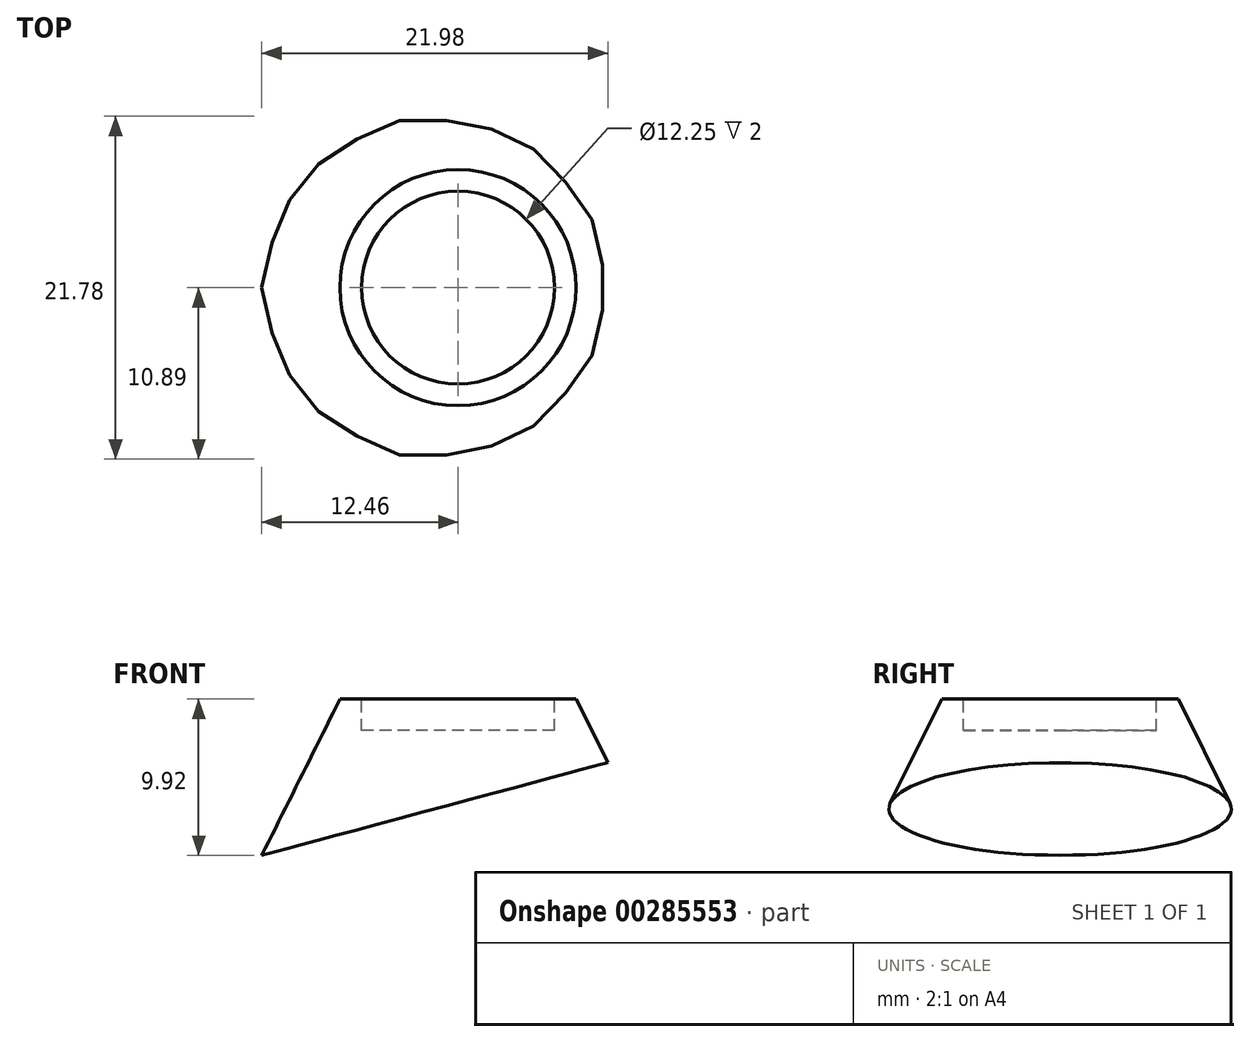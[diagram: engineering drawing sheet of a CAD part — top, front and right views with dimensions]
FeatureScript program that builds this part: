
annotation { "Feature Type Name" : "Feature", "Feature Type Description" : "" }
export const myFeature = defineFeature(function(context is Context, id is Id, definition is map)
    precondition{}
    {
        {
            var Q0;
            Q0=qCreatedBy(makeId("Top.planeOp"),FACE);
            var sketch = newSketch(context, id + "F0", { "sketchPlane" : qUnion([Q0])});
            skCircle(sketch, "E0", {"center": v(0, 0) * mm, "radius": 12.5 * mm});
            skSolve(sketch);
        }
        {
            var Q0;
            Q0=makeQuery(id+"F0.imprint","IMPRINT",FACE,{"disambiguationData":[TD([[makeQuery(id+"F0.imprint","IMPRINT",EDGE,{"derivedFrom":sQuery(id+"F0.wireOp",EDGE,"E0")}),1.0]])]});
            extrude(context, id + "F1", {"entities" : qUnion([Q0]), "depth" : 10 * mm});
        }
        {
            var Q0;
            Q0=makeQuery(id+"F1.opExtrude","CAP_EDGE",EDGE,{"disambiguationData":[OSD([sQuery(id+"F0.wireOp",EDGE,"E0")])],"isStart":false});
            chamfer(context, id + "F2", {"entities" : qUnion([Q0]), "chamferType" : ChamferType.TWO_OFFSETS, "width1" : 5 * mm, "oppositeDirection" : false, "width2" : 10 * mm, "tangentPropagation" : true});
        }
        {
            var Q0;
            Q0=qCreatedBy(makeId("Front.planeOp"),FACE);
            var sketch = newSketch(context, id + "F3", { "sketchPlane" : qUnion([Q0])});
            skLineSegment(sketch, "E1", {"start": v(-12.76, 0) * mm, "end": v(11.72, 6.56) * mm});
            skLineSegment(sketch, "E2", {"start": v(-12.76, 0) * mm, "end": v(-7.28, -3.85) * mm});
            skLineSegment(sketch, "E3", {"start": v(-7.28, -3.85) * mm, "end": v(16.18, -2.42) * mm});
            skLineSegment(sketch, "E4", {"start": v(16.18, -2.42) * mm, "end": v(11.72, 6.56) * mm});
            skSolve(sketch);
        }
        {
            var Q0;
            Q0=makeQuery(id+"F3.imprint","IMPRINT",FACE,{"disambiguationData":[TD([[makeQuery(id+"F3.imprint","IMPRINT",EDGE,{"derivedFrom":sQuery(id+"F3.wireOp",EDGE,"E1")}),-1.0]])]});
            extrude(context, id + "F4", {"entities" : qUnion([Q0]), "operationType" : NewBodyOperationType.REMOVE, "endBound" : BoundingType.SYMMETRIC, "oppositeDirection" : true, "depth" : 25 * mm});
        }
        {
            var Q0;
            Q0=makeQuery(id+"F1.opExtrude","CAP_FACE",FACE,{"disambiguationData":[OSD([sQuery(id+"F0.wireOp",EDGE,"E0")])],"isStart":false});
            var sketch = newSketch(context, id + "F5", { "sketchPlane" : qUnion([Q0])});
            skCircle(sketch, "E5", {"center": v(0, 0) * mm, "radius": 6.12 * mm});
            skSolve(sketch);
        }
        {
            var Q0;
            Q0=makeQuery(id+"F5.imprint","IMPRINT",FACE,{"disambiguationData":[TD([[makeQuery(id+"F5.imprint","IMPRINT",EDGE,{"derivedFrom":sQuery(id+"F5.wireOp",EDGE,"E5")}),1.0]])]});
            extrude(context, id + "F6", {"entities" : qUnion([Q0]), "operationType" : NewBodyOperationType.REMOVE, "oppositeDirection" : true, "depth" : 2 * mm});
        }
    });
